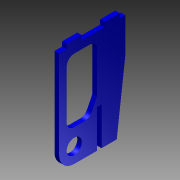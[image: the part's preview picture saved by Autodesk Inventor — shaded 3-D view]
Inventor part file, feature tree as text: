
AUTODESK INVENTOR PART (.ipt)
format: ipt  version: 2012 (Build 160160000, 160)  size: 129,024 bytes
history: native  units: mm
features: extrude x1, sketch x1
ambient origin geometry x8: Origin, YZ Plane, XZ Plane, XY Plane, X Axis, Y Axis, Z Axis, Center Point
feature tree (2):
  extrude  "Extrusion2"  Depth=10.0mm
  sketch  "Sketch1"  dims[d5=50.0mm d6=66.5mm d7=10.0mm d10=5.0mm d12=10.0mm d17=10.0mm d18=3.0mm d20=10.0mm d21=3.0mm d22=5.0mm d23=15.0mm d24=3.0mm d25=3.0mm d42=3.0mm d46=3.75mm d47=22.0mm d49=2.0mm d54=10.0mm d55=15.0mm d57=68.0mm d58=15.75mm d59=25.0mm d61=5.0mm d65=5.0mm d66=10.0mm d67=5.0mm d68=5.0mm d69=3.0mm d70=0.0mm]
